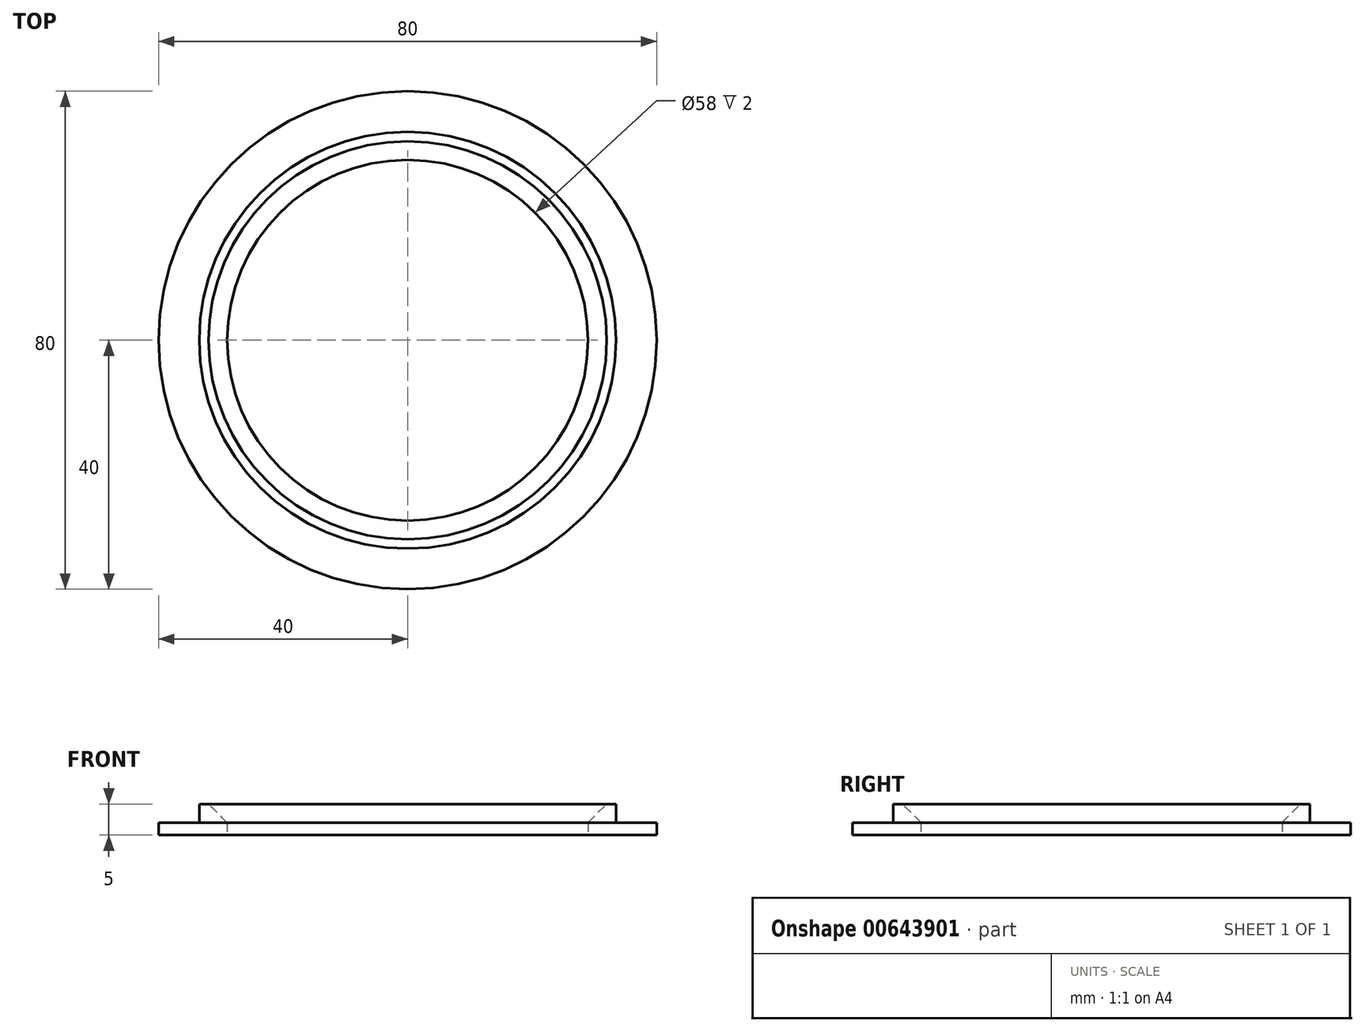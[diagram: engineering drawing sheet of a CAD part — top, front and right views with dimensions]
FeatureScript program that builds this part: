
annotation { "Feature Type Name" : "Feature", "Feature Type Description" : "" }
export const myFeature = defineFeature(function(context is Context, id is Id, definition is map)
    precondition{}
    {
        {
            var Q0;
            Q0=qCreatedBy(makeId("Top.planeOp"),FACE);
            var sketch = newSketch(context, id + "F0", { "sketchPlane" : qUnion([Q0])});
            skCircle(sketch, "E0", {"center": v(0, 0) * mm, "radius": 29 * mm});
            skCircle(sketch, "E1", {"center": v(0, 0) * mm, "radius": 40 * mm});
            skSolve(sketch);
        }
        {
            var Q0;
            Q0 = qSketchRegion(id + "F0", true);
            extrude(context, id + "F1", {"entities" : qUnion([Q0]), "depth" : 2 * mm, "offsetDistance" : 25 * mm});
        }
        {
            var Q0;
            Q0=qCreatedBy(makeId("Front.planeOp"),FACE);
            var sketch = newSketch(context, id + "F2", { "sketchPlane" : qUnion([Q0])});
            skLineSegment(sketch, "E2", {"start": v(28.97, 2) * mm, "end": v(31.97, 2) * mm});
            skLineSegment(sketch, "E3", {"start": v(31.97, 5) * mm, "end": v(28.97, 2) * mm});
            skLineSegment(sketch, "E4", {"start": v(0, 0) * mm, "end": v(0, 8.32) * mm, "construction": true});
            skLineSegment(sketch, "E5", {"start": v(31.97, 5) * mm, "end": v(33.47, 5) * mm});
            skLineSegment(sketch, "E6", {"start": v(33.47, 5) * mm, "end": v(33.47, 2) * mm});
            skLineSegment(sketch, "E7", {"start": v(33.47, 2) * mm, "end": v(31.97, 2) * mm});
            skSolve(sketch);
        }
        {
            var Q0;
            Q0=makeQuery(id+"F2.imprint","IMPRINT",FACE,{"disambiguationData":[TD([[makeQuery(id+"F2.imprint","IMPRINT",EDGE,{"derivedFrom":sQuery(id+"F2.wireOp",EDGE,"E2")}),1.0]])]});
            var Q1;
            Q1=sQuery(id+"F2.wireOp",EDGE,"E4");
            var Q2;
            Q2=sQuery(id+"F2.wireOp",EDGE,"E3");
            var Q3;
            Q3=sQuery(id+"F2.wireOp",EDGE,"E2");
            var Q4;
            Q4=sQuery(id+"F2.wireOp",EDGE,"E5");
            var Q5;
            Q5=sQuery(id+"F2.wireOp",EDGE,"E7");
            var Q6;
            Q6=sQuery(id+"F2.wireOp",EDGE,"E6");
            var Q7;
            Q7=sQuery(id+"F2.wireOp",EDGE,"E4");
            revolve(context, id + "F3", {"operationType" : NewBodyOperationType.ADD, "entities" : qUnion([Q0]), "surfaceEntities" : qUnion([Q1, Q2, Q3, Q4, Q5, Q6]), "axis" : qUnion([Q7]), "revolveType" : RevolveType.FULL});
        }
    });
